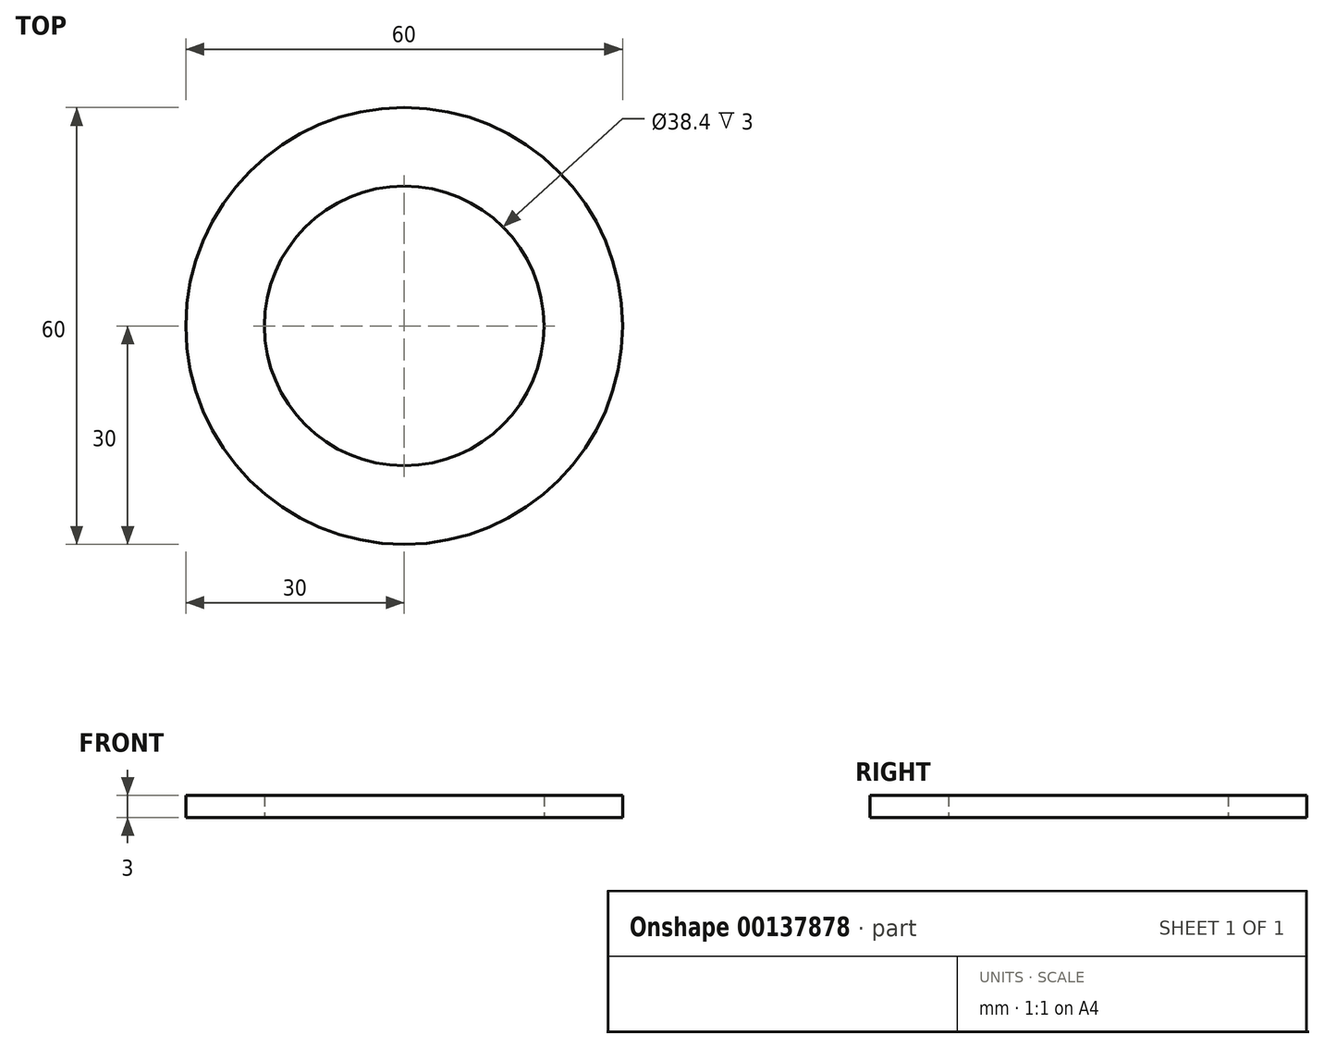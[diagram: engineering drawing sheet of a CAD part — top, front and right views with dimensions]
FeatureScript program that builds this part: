
annotation { "Feature Type Name" : "Feature", "Feature Type Description" : "" }
export const myFeature = defineFeature(function(context is Context, id is Id, definition is map)
    precondition{}
    {
        {
            var Q0;
            Q0=qCreatedBy(makeId("Top.planeOp"),FACE);
            var sketch = newSketch(context, id + "F0", { "sketchPlane" : qUnion([Q0])});
            skCircle(sketch, "E0", {"center": v(0, 0) * mm, "radius": 19.2 * mm});
            skCircle(sketch, "E1", {"center": v(0, 0) * mm, "radius": 30 * mm});
            skSolve(sketch);
        }
        {
            var Q0;
            Q0=makeQuery(id+"F0.imprint","IMPRINT",FACE,{"disambiguationData":[TD([[makeQuery(id+"F0.imprint","IMPRINT",EDGE,{"derivedFrom":sQuery(id+"F0.wireOp",EDGE,"E0")}),-1.0]])]});
            extrude(context, id + "F1", {"entities" : qUnion([Q0]), "depth" : 3 * mm});
        }
    });
